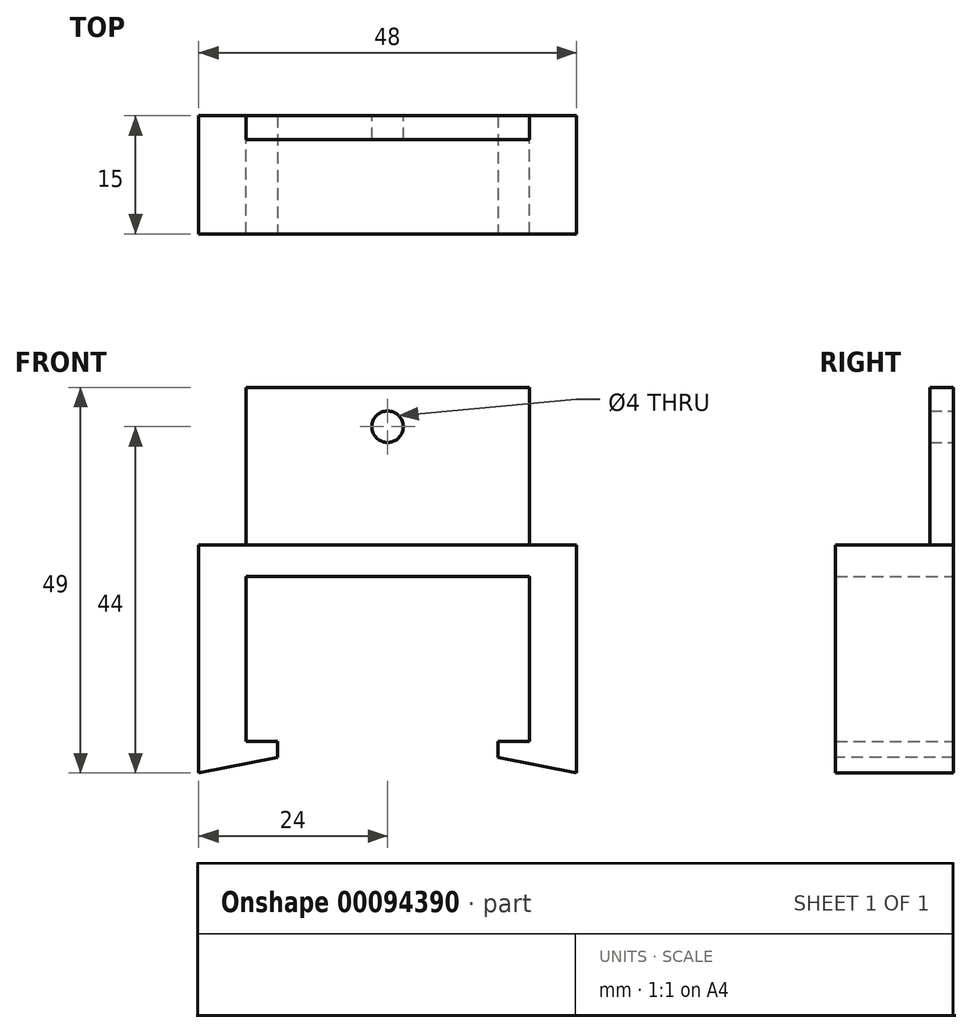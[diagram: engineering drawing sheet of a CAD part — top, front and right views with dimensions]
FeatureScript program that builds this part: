
annotation { "Feature Type Name" : "Feature", "Feature Type Description" : "" }
export const myFeature = defineFeature(function(context is Context, id is Id, definition is map)
    precondition{}
    {
        {
            var Q0;
            Q0=qCreatedBy(makeId("Top.planeOp"),FACE);
            var sketch = newSketch(context, id + "F0", { "sketchPlane" : qUnion([Q0])});
            skLineSegment(sketch, "E0.bottom", {"start": v(-18, -15) * mm, "end": v(18, -15) * mm});
            skLineSegment(sketch, "E0.top", {"start": v(-18, 0) * mm, "end": v(18, 0) * mm});
            skLineSegment(sketch, "E0.left", {"start": v(-18, -15) * mm, "end": v(-18, 0) * mm});
            skLineSegment(sketch, "E0.right", {"start": v(18, -15) * mm, "end": v(18, 0) * mm});
            skLineSegment(sketch, "E1", {"start": v(0, 0) * mm, "end": v(0, -15) * mm, "construction": true});
            skLineSegment(sketch, "E2", {"start": v(-18, -15) * mm, "end": v(-24, -15) * mm});
            skLineSegment(sketch, "E3", {"start": v(-18, 0) * mm, "end": v(-24, 0) * mm});
            skLineSegment(sketch, "E4", {"start": v(-24, 0) * mm, "end": v(-24, -15) * mm});
            skLineSegment(sketch, "E5.MirrorCS", {"start": v(18, -15) * mm, "end": v(24, -15) * mm});
            skLineSegment(sketch, "E6.MirrorCS", {"start": v(24, 0) * mm, "end": v(24, -15) * mm});
            skLineSegment(sketch, "E7.MirrorCS", {"start": v(18, 0) * mm, "end": v(24, 0) * mm});
            skSolve(sketch);
        }
        {
            var Q0;
            Q0=makeQuery(id+"F0.imprint","IMPRINT",FACE,{"disambiguationData":[TD([[makeQuery(id+"F0.imprint","IMPRINT",EDGE,{"derivedFrom":sQuery(id+"F0.wireOp",EDGE,"E0.left")}),1.0]])]});
            var Q1;
            Q1=makeQuery(id+"F0.imprint","IMPRINT",FACE,{"disambiguationData":[TD([[makeQuery(id+"F0.imprint","IMPRINT",EDGE,{"derivedFrom":sQuery(id+"F0.wireOp",EDGE,"E0.bottom")}),1.0]])]});
            var Q2;
            Q2=makeQuery(id+"F0.imprint","IMPRINT",FACE,{"disambiguationData":[TD([[makeQuery(id+"F0.imprint","IMPRINT",EDGE,{"derivedFrom":sQuery(id+"F0.wireOp",EDGE,"E0.right")}),-1.0]])]});
            extrude(context, id + "F1", {"entities" : qUnion([Q0, Q1, Q2]), "oppositeDirection" : true, "depth" : 4 * mm});
        }
        {
            var Q0;
            Q0=makeQuery(id+"F0.imprint","IMPRINT",FACE,{"disambiguationData":[TD([[makeQuery(id+"F0.imprint","IMPRINT",EDGE,{"derivedFrom":sQuery(id+"F0.wireOp",EDGE,"E0.left")}),1.0]])]});
            var Q1;
            Q1=makeQuery(id+"F0.imprint","IMPRINT",FACE,{"disambiguationData":[TD([[makeQuery(id+"F0.imprint","IMPRINT",EDGE,{"derivedFrom":sQuery(id+"F0.wireOp",EDGE,"E0.right")}),-1.0]])]});
            extrude(context, id + "F2", {"entities" : qUnion([Q0, Q1]), "operationType" : NewBodyOperationType.ADD, "oppositeDirection" : true, "depth" : 25 * mm});
        }
        {
            var Q0;
            {var subQ0=sQuery(id+"F0.wireOp",EDGE,"E5.MirrorCS");var subQ1=sQuery(id+"F0.wireOp",EDGE,"E2");Q0=makeQuery(id+"F2.boolean.opBoolean","MERGE",FACE,{"derivedFrom":[makeQuery(id+"F1.opExtrude","SWEPT_FACE",FACE,{"disambiguationData":[OSD([sQuery(id+"F0.wireOp",EDGE,"E0.bottom"),subQ1,subQ0])]}),makeQuery(id+"F2.opExtrude","SWEPT_FACE",FACE,{"disambiguationData":[OSD([subQ1])]}),makeQuery(id+"F2.opExtrude","SWEPT_FACE",FACE,{"disambiguationData":[OSD([subQ0])]})]});}
            var sketch = newSketch(context, id + "F3", { "sketchPlane" : qUnion([Q0])});
            skLineSegment(sketch, "E8", {"start": v(-24, -25) * mm, "end": v(-24, -29) * mm});
            skLineSegment(sketch, "E9", {"start": v(-24, -29) * mm, "end": v(-14, -27) * mm});
            skLineSegment(sketch, "E10", {"start": v(-18, -25) * mm, "end": v(-14, -25) * mm});
            skLineSegment(sketch, "E11", {"start": v(-14, -25) * mm, "end": v(-14, -27) * mm});
            skLineSegment(sketch, "E12", {"start": v(-18, -25) * mm, "end": v(18, -25) * mm, "construction": true});
            skLineSegment(sketch, "E13", {"start": v(0, 0) * mm, "end": v(0, -25) * mm, "construction": true});
            skLineSegment(sketch, "E14.MirrorCS", {"start": v(24, -25) * mm, "end": v(24, -29) * mm});
            skLineSegment(sketch, "E15.MirrorCS", {"start": v(18, -25) * mm, "end": v(14, -25) * mm});
            skLineSegment(sketch, "E16.MirrorCS", {"start": v(14, -25) * mm, "end": v(14, -27) * mm});
            skLineSegment(sketch, "E17.MirrorCS", {"start": v(24, -29) * mm, "end": v(14, -27) * mm});
            skSolve(sketch);
        }
        {
            var Q0;
            Q0=makeQuery(id+"F3.imprint","IMPRINT",FACE,{"disambiguationData":[TD([[makeQuery(id+"F3.imprint","IMPRINT",EDGE,{"derivedFrom":sQuery(id+"F3.wireOp",EDGE,"E14.MirrorCS")}),-1.0]])]});
            var Q1;
            Q1=makeQuery(id+"F3.imprint","IMPRINT",FACE,{"disambiguationData":[TD([[makeQuery(id+"F3.imprint","IMPRINT",EDGE,{"derivedFrom":sQuery(id+"F3.wireOp",EDGE,"E8")}),1.0]])]});
            var Q2;
            {var subQ0=sQuery(id+"F0.wireOp",EDGE,"E7.MirrorCS");var subQ1=sQuery(id+"F0.wireOp",EDGE,"E3");Q2=makeQuery(id+"F2.boolean.opBoolean","MERGE",FACE,{"derivedFrom":[makeQuery(id+"F1.opExtrude","SWEPT_FACE",FACE,{"disambiguationData":[OSD([sQuery(id+"F0.wireOp",EDGE,"E0.top"),subQ1,subQ0])]}),makeQuery(id+"F2.opExtrude","SWEPT_FACE",FACE,{"disambiguationData":[OSD([subQ1])]}),makeQuery(id+"F2.opExtrude","SWEPT_FACE",FACE,{"disambiguationData":[OSD([subQ0])]})]});}
            extrude(context, id + "F4", {"entities" : qUnion([Q0, Q1]), "operationType" : NewBodyOperationType.ADD, "endBound" : BoundingType.UP_TO_SURFACE, "oppositeDirection" : true, "endBoundEntityFace" : qUnion([Q2]), "depth" : 25 * mm});
        }
        {
            var Q0;
            Q0=qCreatedBy(makeId("Top.planeOp"),FACE);
            var sketch = newSketch(context, id + "F5", { "sketchPlane" : qUnion([Q0])});
            skLineSegment(sketch, "E18.0", {"start": v(-18, 0) * mm, "end": v(18, 0) * mm});
            skLineSegment(sketch, "E19", {"start": v(-18, 0) * mm, "end": v(-18, -3) * mm});
            skLineSegment(sketch, "E20", {"start": v(18, 0) * mm, "end": v(18, -3) * mm});
            skLineSegment(sketch, "E21", {"start": v(-18, -3) * mm, "end": v(18, -3) * mm});
            skSolve(sketch);
        }
        {
            var Q0;
            Q0 = qSketchRegion(id + "F5", true);
            extrude(context, id + "F6", {"entities" : qUnion([Q0]), "operationType" : NewBodyOperationType.ADD, "depth" : 20 * mm});
        }
        {
            var Q0;
            {var subQ0=sQuery(id+"F0.wireOp",EDGE,"E7.MirrorCS");var subQ1=sQuery(id+"F0.wireOp",EDGE,"E3");Q0=makeQuery(id+"F6.boolean.opBoolean","MERGE",FACE,{"derivedFrom":[makeQuery(id+"F4.boolean.opBoolean","MERGE",FACE,{"derivedFrom":[makeQuery(id+"F2.boolean.opBoolean","MERGE",FACE,{"derivedFrom":[makeQuery(id+"F1.opExtrude","SWEPT_FACE",FACE,{"disambiguationData":[OSD([sQuery(id+"F0.wireOp",EDGE,"E0.top"),subQ1,subQ0])]}),makeQuery(id+"F2.opExtrude","SWEPT_FACE",FACE,{"disambiguationData":[OSD([subQ1])]}),makeQuery(id+"F2.opExtrude","SWEPT_FACE",FACE,{"disambiguationData":[OSD([subQ0])]})]}),makeQuery(id+"F4.opExtrude","CAP_FACE",FACE,{"disambiguationData":[OSD([sQuery(id+"F0.wireOp",EDGE,"E2"),sQuery(id+"F3.wireOp",EDGE,"E8"),sQuery(id+"F3.wireOp",EDGE,"E9"),sQuery(id+"F3.wireOp",EDGE,"E10"),sQuery(id+"F3.wireOp",EDGE,"E11")])],"isStart":false}),makeQuery(id+"F4.opExtrude","CAP_FACE",FACE,{"disambiguationData":[OSD([sQuery(id+"F0.wireOp",EDGE,"E5.MirrorCS"),sQuery(id+"F3.wireOp",EDGE,"E14.MirrorCS"),sQuery(id+"F3.wireOp",EDGE,"E15.MirrorCS"),sQuery(id+"F3.wireOp",EDGE,"E16.MirrorCS"),sQuery(id+"F3.wireOp",EDGE,"E17.MirrorCS")])],"isStart":false})]}),makeQuery(id+"F6.opExtrude","SWEPT_FACE",FACE,{"disambiguationData":[OSD([sQuery(id+"F5.wireOp",EDGE,"E18.0")])]})]});}
            var sketch = newSketch(context, id + "F7", { "sketchPlane" : qUnion([Q0])});
            skLineSegment(sketch, "E22", {"start": v(0, 0) * mm, "end": v(0, 15) * mm, "construction": true});
            skCircle(sketch, "E23", {"center": v(0, 15) * mm, "radius": 2 * mm});
            skSolve(sketch);
        }
        {
            var Q0;
            Q0=makeQuery(id+"F7.imprint","IMPRINT",FACE,{"disambiguationData":[TD([[makeQuery(id+"F7.imprint","IMPRINT",EDGE,{"derivedFrom":sQuery(id+"F7.wireOp",EDGE,"E23")}),1.0]])]});
            var Q1;
            Q1=makeQuery(id+"F6.opExtrude","SWEPT_FACE",FACE,{"disambiguationData":[OSD([sQuery(id+"F5.wireOp",EDGE,"E21")])]});
            extrude(context, id + "F8", {"entities" : qUnion([Q0]), "operationType" : NewBodyOperationType.REMOVE, "endBound" : BoundingType.UP_TO_SURFACE, "oppositeDirection" : true, "endBoundEntityFace" : qUnion([Q1]), "depth" : 25 * mm});
        }
    });
